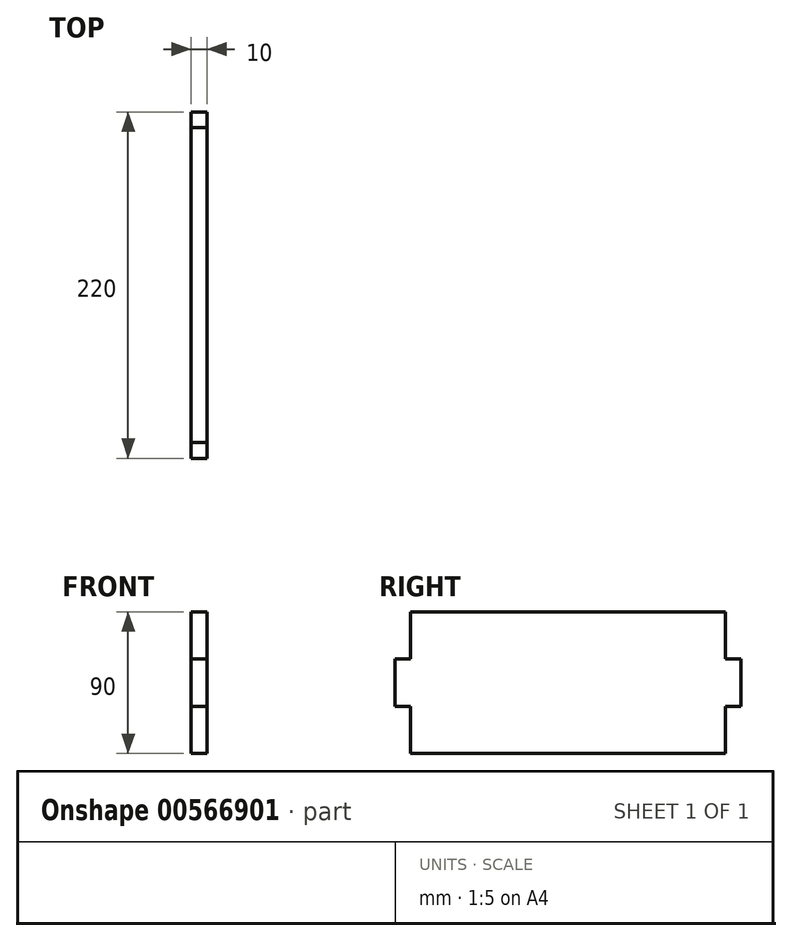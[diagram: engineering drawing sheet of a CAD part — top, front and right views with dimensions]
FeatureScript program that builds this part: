
annotation { "Feature Type Name" : "Feature", "Feature Type Description" : "" }
export const myFeature = defineFeature(function(context is Context, id is Id, definition is map)
    precondition{}
    {
        {
            var Q0;
            Q0=qCreatedBy(makeId("Right.planeOp"),FACE);
            var sketch = newSketch(context, id + "F0", { "sketchPlane" : qUnion([Q0])});
            skLineSegment(sketch, "E0", {"start": v(0, 0) * mm, "end": v(0, 30) * mm});
            skLineSegment(sketch, "E1", {"start": v(0, 30) * mm, "end": v(-10, 30) * mm});
            skLineSegment(sketch, "E2", {"start": v(-10, 30) * mm, "end": v(-10, 60) * mm});
            skLineSegment(sketch, "E3", {"start": v(-10, 60) * mm, "end": v(0, 60) * mm});
            skLineSegment(sketch, "E4", {"start": v(0, 60) * mm, "end": v(0, 90) * mm});
            skLineSegment(sketch, "E5", {"start": v(0, 90) * mm, "end": v(100, 90) * mm});
            skLineSegment(sketch, "E6", {"start": v(100, 0) * mm, "end": v(0, 0) * mm});
            skLineSegment(sketch, "E7", {"start": v(100, 90) * mm, "end": v(100, 0) * mm, "construction": true});
            skLineSegment(sketch, "E8.MirrorCS", {"start": v(210, 60) * mm, "end": v(200, 60) * mm});
            skLineSegment(sketch, "E9.MirrorCS", {"start": v(200, 0) * mm, "end": v(200, 30) * mm});
            skLineSegment(sketch, "E10.MirrorCS", {"start": v(200, 30) * mm, "end": v(210, 30) * mm});
            skLineSegment(sketch, "E11.MirrorCS", {"start": v(210, 30) * mm, "end": v(210, 60) * mm});
            skLineSegment(sketch, "E12.MirrorCS", {"start": v(100, 0) * mm, "end": v(200, 0) * mm});
            skLineSegment(sketch, "E13.MirrorCS", {"start": v(200, 60) * mm, "end": v(200, 90) * mm});
            skLineSegment(sketch, "E14.MirrorCS", {"start": v(200, 90) * mm, "end": v(100, 90) * mm});
            skSolve(sketch);
        }
        {
            var Q0;
            Q0=makeQuery(id+"F0.imprint","IMPRINT",FACE,{"disambiguationData":[TD([[makeQuery(id+"F0.imprint","IMPRINT",EDGE,{"derivedFrom":sQuery(id+"F0.wireOp",EDGE,"E0")}),-1.0]])]});
            extrude(context, id + "F1", {"entities" : qUnion([Q0]), "depth" : 10 * mm, "offsetDistance" : 25 * mm});
        }
    });
